# Revit family: LAMP_KOMBIC 150 SURFACE 2000 CRI80 OPAL DALI
name_source: partatom
category: Luminarias
revit_build: Autodesk Revit 2018 (Build: 20190510_1515(x64)
units: mm (PartAtom-declared; Revit-internal decimal feet)

## family parameters
Anfitrión = Cara
Compartido = No
Corte con vacíos al cargar = No
Cota de conector redondo = Diámetro de uso
Origen de luz = Sí
Punto de cálculo de habitación = No
Tipo de pieza = Normal

## types (12) — shared parameters
CRI = 80
Cambio de temperatura de color de luz atenuada = <Ninguno>
Diameter = 150 mm
Elevación por defecto = 1219 mm
Fabricante = LAMP
Filtro de color = 16777215
Gear = Adjustable DALI
Height = 180 mm  [stored 0.590551 ft]
IEE = A+
Installation instructions = https://www.lamp.es
Insulation class = II
LED Lifetime = 50.000 L90 B10
Lamp = COB LED
Last update = 02/09/2021
Luminaire type = Suspended
MacAdam = 3
Manufacturer URL = http://www.lamp.es
Manufacturer country = Spain
Manufacturer name = LAMP
Material cable suspension = LAMP_Acero genérico
Material difusor = LAMP_PMMA Difusor Kombic
Model explanation = Possibility of chossing between surface or suspended within the model
Plum = 14 W
Power = 12 W
Power Supply = 220-240V 50/60Hz
Product URL = https://www.lamp.es
Product datasheet = http://www.lamp.es
Protection rating = IP40
Type = COB PHILIPS
Weight = 1.48 kg
Ángulo de inclinación = -90.00°

## per-type parameters (varying)
| type | Archivo de red fotométrica | Efficacy | Finish | Material cuerpo | Material floron | Material reflector | Modelo | Product code |
| 1427LM 3000K  M/B | K21SF2040OP830NMB.IES | 101 lm/W | Matte black RAL 9011 | LAMP_Plástico genérico NG | LAMP_Plástico genérico NG | LAMP_PC Reflector Kombic Metalizado Mate | K21SF2040OP830DMB | K21SF2040OP830DMB |
| 1427LM 3000K  M/W | K21SF2040OP830NMW.IES | 101 lm/W | Matte white RAL 9010 | LAMP_Plástico genérico BL | LAMP_Plástico genérico BL | LAMP_PC Reflector Kombic Metalizado Mate | K21SF2040OP830DMW | K21SF2040OP830DMW |
| 1473LM 3000K  W/B | K21SF2040OP830NWB.IES | 104 lm/W | Matte black RAL 9011 | LAMP_Plástico genérico NG | LAMP_Plástico genérico NG | LAMP_PC Reflector Kombic Blanco | K21SF2040OP830DWB | K21SF2040OP830DWB |
| 1473LM 3000K  W/W | K21SF2040OP830NWW.IES | 104 lm/W | Matte white RAL 9010 | LAMP_Plástico genérico BL | LAMP_Plástico genérico BL | LAMP_PC Reflector Kombic Blanco | K21SF2040OP830DWW | K21SF2040OP830DWW |
| 1486LM 4000K  M/B | K21SF2040OP840NMB.IES | 105 lm/W | Matte black RAL 9011 | LAMP_Plástico genérico NG | LAMP_Plástico genérico NG | LAMP_PC Reflector Kombic Metalizado Mate | K21SF2040OP840DMB | K21SF2040OP840DMB |
| 1486LM 4000K  M/W | K21SF2040OP840NMW.IES | 105 lm/W | Matte white RAL 9010 | LAMP_Plástico genérico BL | LAMP_Plástico genérico BL | LAMP_PC Reflector Kombic Metalizado Mate | K21SF2040OP840DMW | K21SF2040OP840DMW |
| 1488LM 3000K  BR/B | K21SF2040OP830NRB.IES | 106 lm/W | Matte black RAL 9011 | LAMP_Plástico genérico NG | LAMP_Plástico genérico NG | LAMP_PC Reflector Kombic Metalizado Brillante | K21SF2040OP830DRB | K21SF2040OP830DRB |
| 1488LM 3000K  BR/W | K21SF2040OP830NRW.IES | 106 lm/W | Matte white RAL 9010 | LAMP_Plástico genérico BL | LAMP_Plástico genérico BL | LAMP_PC Reflector Kombic Metalizado Brillante | K21SF2040OP830DRW | K21SF2040OP830DRW |
| 1534LM 4000K  W/B | K21SF2040OP840NWB.IES | 109 lm/W | Matte black RAL 9011 | LAMP_Plástico genérico NG | LAMP_Plástico genérico NG | LAMP_PC Reflector Kombic Blanco | K21SF2040OP840DWB | K21SF2040OP840DWB |
| 1534LM 4000K  W/W | K21SF2040OP840NWW.IES | 109 lm/W | Matte white RAL 9010 | LAMP_Plástico genérico BL | LAMP_Plástico genérico BL | LAMP_PC Reflector Kombic Blanco | K21SF2040OP840DWW | K21SF2040OP840DWW |
| 1550LM 4000K  BR/B | K21SF2040OP840NRB.IES | 110 lm/W | Matte black RAL 9011 | LAMP_Plástico genérico NG | LAMP_Plástico genérico NG | LAMP_PC Reflector Kombic Metalizado Brillante | K21SF2040OP840DRB | K21SF2040OP840DRB |
| 1550LM 4000K  BR/W | K21SF2040OP840NRW.IES | 110 lm/W | Matte white RAL 9010 | LAMP_Plástico genérico BL | LAMP_Plástico genérico BL | LAMP_PC Reflector Kombic Metalizado Brillante | K21SF2040OP840DRW | K21SF2040OP840DRW |

note: [stored X ft] marks values corroborated as IEEE doubles in the binary element streams (Revit-internal decimal feet)
